# Revit family: PANES-2X4
name_source: partatom
category: Generic Models
units: mm (PartAtom-declared; Revit-internal decimal feet)

## family parameters
Always vertical = Yes
Can host rebar = No
Cut with Voids When Loaded = No
Maintain Annotation Orientation = No
Part Type = Normal
Room Calculation Point = No
Round Connector Dimension = Use Diameter
Shared = No
Work Plane-Based = No

## types (9) — shared parameters
Default Elevation = 0' - 0"
Manufacturer = Acoustical Surfaces, Inc.
Material = Envirocoustic Wood Wool
Thickness = 0' - 1"
URL = https://www.acousticalsurfaces.com

## per-type parameters (varying)
| type | Backer | Backer Thickness | Finish |
| STANDARD - CUSTOM PAINTED | No | 0' - 1" | Custom Painted |
| STANDARD - PRIMED WHITE | No | 0' - 1" | Primed White |
| STANDARD - PRIMED CLEAR | No | 0' - 1" | Primed Clear |
| 2 INCH CFAB BACKER - PRIMED WHITE | Yes | 0' - 2" | Primed White |
| 1 INCH CFAB BACKER - PRIMED WHITE | Yes | 0' - 1" | Primed White |
| 2 INCH CFAB BACKER - PRIMED CLEAR | Yes | 0' - 2" | Primed Clear |
| 1 INCH CFAB BACKER - PRIMED CLEAR | Yes | 0' - 1" | Primed Clear |
| 2 INCH CFAB BACKER - CUSTOM PAINTED | Yes | 0' - 2" | Custom Painted |
| 1 INCH CFAB BACKER - CUSTOM PAINTED | Yes | 0' - 1" | Custom Painted |

## geometry (parser evidence)
native form markers: Sweep x4
no freeform markers — native parametric forms only
